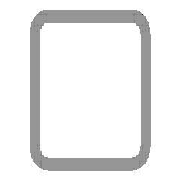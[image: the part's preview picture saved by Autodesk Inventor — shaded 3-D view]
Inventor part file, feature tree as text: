
AUTODESK INVENTOR PART (.ipt)
format: ipt  version: 2022 (Build 260153000, 153)  size: 132,608 bytes
history: native  units: mm (DEFAULTED — no unit token found)
features: other x4, sketch x3, plane x1
ambient origin geometry x8: Origin, YZ Plane, XZ Plane, XY Plane, X Axis, Y Axis, Z Axis, Center Point
bodies: Solid1 (feature_tree), Body (feature_tree)
feature tree (8):
  parser-record x1  (decoder bookkeeping rows leaked as tree rows — omitted from the tree; the rows remain in map.json)
  other  "Driven Length"
  other  "Start Plane"
  other  "End Plane"
  sketch  "Sketch"  dims[d7=8.0mm d9=40.0mm d11=40.0mm d12=4.0mm d13=-0.0mm d14=240.0mm d15=20.0mm d16=20.0mm d17=90.0deg d18=240.0mm]
  sketch  "Sketch3"  dims[d3=240.0mm]
  plane  "Work Plane3"
  sketch  "Sketch4"  dims[d4=0.0mm]
